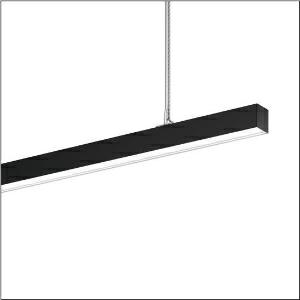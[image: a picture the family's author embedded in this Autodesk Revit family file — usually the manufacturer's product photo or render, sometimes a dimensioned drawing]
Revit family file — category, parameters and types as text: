
# Revit family: silica_r__21_51mx33dc4dbb_4870
name_source: partatom
category: Lighting Fixtures
units: mm (PartAtom-declared; Revit-internal decimal feet)

## family parameters
Cut with Voids When Loaded = No
Host = Face
Light Source = No
Part Type = Normal
Room Calculation Point = No
Round Connector Dimension = Use Diameter
Shared = No

## types (1)
- --- (1 x LED, 14790 lm, 93.9 W, 4000K)
    Apparent Load = 94 VA
    CIE Flux Codes = 78 96 99 55 100
    Color Rendering = 80
    Color Temperature = 4000K
    Default Elevation = 1800 mm
    Description = Silica® 21, office luminaire, primary optical cover: prismatic diffuser, of PMMA, CAT 2 (L<= 3000cd/m²), light emission: direct/indirect distribution, primary light characteristic: symmetric, installation type: suspended mounting, LED, rated luminous flux: 14.790lm, luminous efficacy: 158lm/W, light colour: 840, colour temperature: 4000K, with terminal, 3+2-pole, max. 2.5mm², mains connection: 220..240V, AC, 50/60Hz, rated input power: 93.9W, luminaire housing, of aluminium, jet black (RAL 9005), length: 3.004mm, width: 53mm, height: 53mm, protection rating (complete): IP20, insulation class (complete): insulation class I (protective earthing), certification: CE, permissible operating ambient temperature: 0..+35°C, standard: EN 50419, packaging unit: 1 piece
    Height = 53 mm
    Lamp = 1 x LED
    Lamp Light Flux = 14790 lm
    Lamp Power = 93.9 W
    Lamp count = 1
    Length = 3004 mm
    Luminous efficacy = 158 lm/W
    Manufacturer = Siteco
    ModVariant = No
    Model = 51MX33DC4DBB
    Mounting Place = Ceiling
    Mounting Type = Pendant
    Number of Poles = 1
    OnlyDefault = Yes
    Power Factor = 1
    Product Name = Silica® 21
    Product group = office luminaire | ceiling pendant
    ProductGroupID = 902
    Protection Class = Protection class I
    Protection Degree = IP 20
    RLX_Detail_Level = 1
    RLX_Emergency_Light_Flux = 0 lm
    RLX_Emergency_Type = 0
    RLX_Emergency_Type_DB = No
    RlxData = <blob elided: 26073 chars, md5=ca27db69>
    Socket = socket
    Standby Power = 0 W
    System Light Flux = 14790 lm
    System Power = 94 W
    Type Comments = factory setting: luminous flux: 100 % | dim-lin: 254 | 323 mA
    Type Image = l_1313646.jpg
    URL = http://relux.com
    VarID = @adj_067187
    Voltage = 0 V
    Weight = 0.00 kg
    Width = 53 mm

## geometry (parser evidence)
native form markers: Blend x4, Sweep x15
no freeform markers — native parametric forms only
